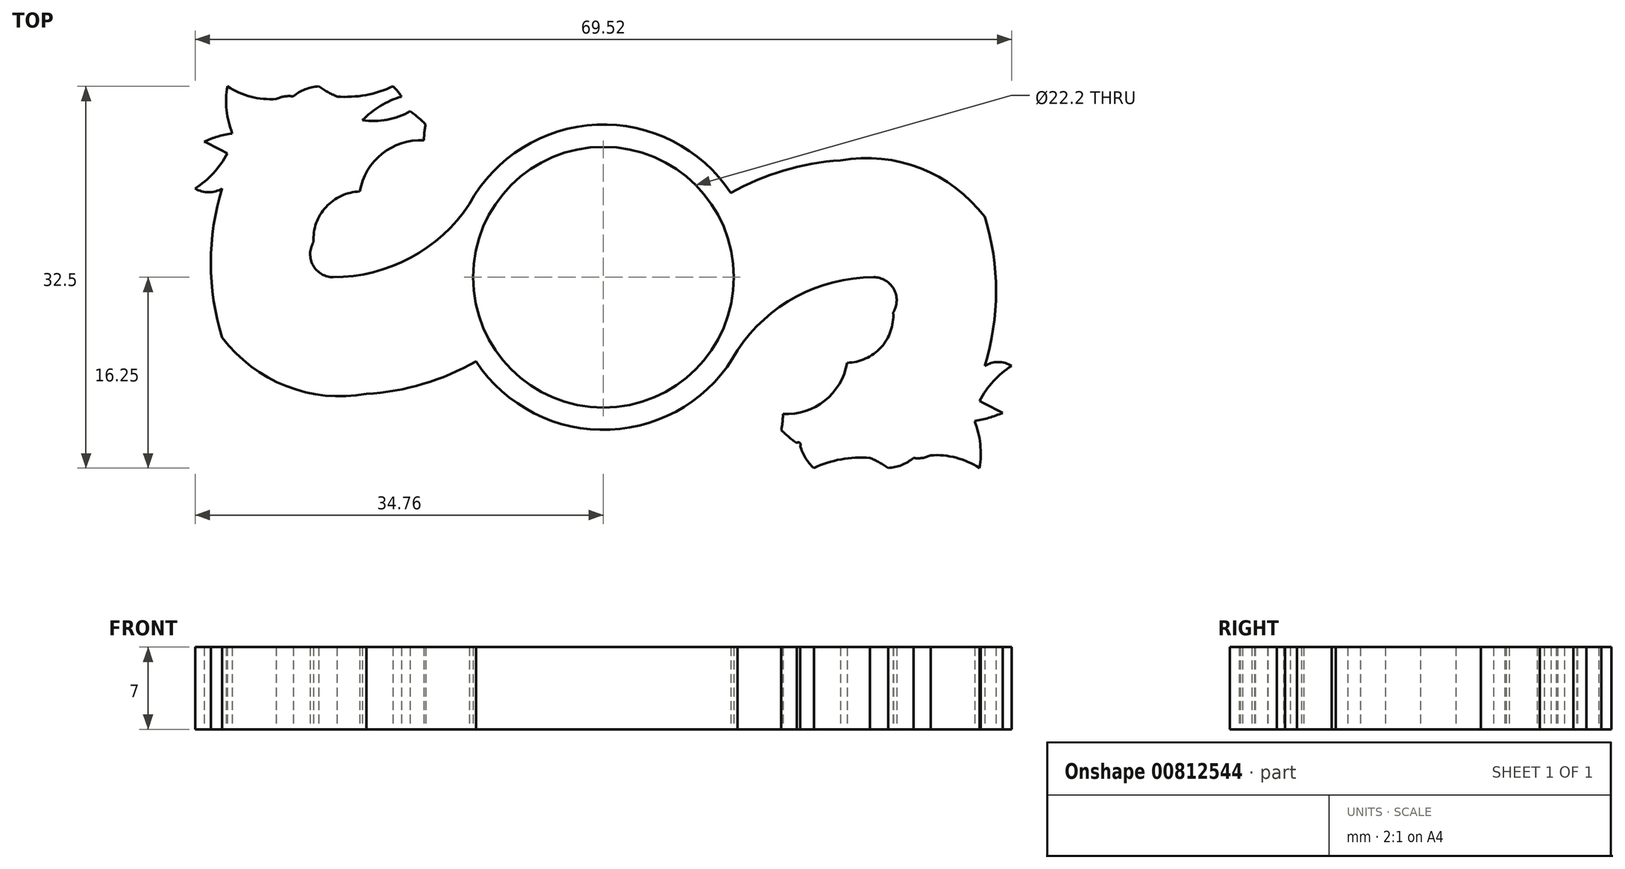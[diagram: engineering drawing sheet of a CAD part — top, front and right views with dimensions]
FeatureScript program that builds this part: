
annotation { "Feature Type Name" : "Feature", "Feature Type Description" : "" }
export const myFeature = defineFeature(function(context is Context, id is Id, definition is map)
    precondition{}
    {
        {
            var Q0;
            Q0=qCreatedBy(makeId("Top.planeOp"),FACE);
            var sketch = newSketch(context, id + "F0", { "sketchPlane" : qUnion([Q0])});
            skCircle(sketch, "E0", {"center": v(0, 0) * mm, "radius": 11.1 * mm});
            skArc(sketch, "E1", {"start": v(-10.84, -7.17) * mm, "mid": v(0.56, -12.99) * mm, "end": v(11.42, -6.21) * mm});
            skPoint(sketch, "E2.center.orphan", {"position": v(-24.05, 0) * mm});
            skEllipticalArc(sketch, "E3", {});
            skEllipticalArc(sketch, "E4", {});
            skEllipticalArc(sketch, "E5.trimOffspring", {});
            skArc(sketch, "E6", {"start": v(-23, 0) * mm, "mid": v(-16.43, 1.65) * mm, "end": v(-11.42, 6.21) * mm});
            skArc(sketch, "E7", {"start": v(-15.28, 11.65) * mm, "mid": v(-18.84, 10.51) * mm, "end": v(-20.74, 7.3) * mm});
            skArc(sketch, "E8", {"start": v(-24.67, 3) * mm, "mid": v(-24.72, 1) * mm, "end": v(-23, 0) * mm});
            skArc(sketch, "E9", {"start": v(-20.74, 7.3) * mm, "mid": v(-23.62, 5.98) * mm, "end": v(-24.67, 3) * mm});
            skArc(sketch, "E10", {"start": v(-17.2, 15.38) * mm, "mid": v(-17.52, 15.84) * mm, "end": v(-17.9, 16.25) * mm});
            skArc(sketch, "E11", {"start": v(-22.68, 15.38) * mm, "mid": v(-20.24, 15.5) * mm, "end": v(-17.9, 16.25) * mm});
            skPoint(sketch, "E11.startSnap0", {"position": v(-17.2, 15.38) * mm});
            skArc(sketch, "E12", {"start": v(-24.25, 16.25) * mm, "mid": v(-23.48, 15.78) * mm, "end": v(-22.68, 15.38) * mm});
            skArc(sketch, "E13", {"start": v(-24.25, 16.25) * mm, "mid": v(-25.39, 16) * mm, "end": v(-26.39, 15.4) * mm});
            skArc(sketch, "E14", {"start": v(-26.39, 15.4) * mm, "mid": v(-27.14, 15.4) * mm, "end": v(-27.85, 15.17) * mm});
            skArc(sketch, "E15", {"start": v(-32.01, 16.25) * mm, "mid": v(-30.02, 15.37) * mm, "end": v(-27.85, 15.17) * mm});
            skArc(sketch, "E16", {"start": v(-32.01, 16.25) * mm, "mid": v(-32.08, 14.21) * mm, "end": v(-31.6, 12.24) * mm});
            skEllipticalArc(sketch, "E17.trimOffspring", {});
            skArc(sketch, "E18", {"start": v(-31.6, 12.24) * mm, "mid": v(-32.82, 11.98) * mm, "end": v(-34, 11.54) * mm});
            skArc(sketch, "E19", {"start": v(-32.01, 10.53) * mm, "mid": v(-33, 11.05) * mm, "end": v(-34, 11.54) * mm});
            skArc(sketch, "E20", {"start": v(-34.76, 7.55) * mm, "mid": v(-33.2, 8.87) * mm, "end": v(-32.01, 10.53) * mm});
            skArc(sketch, "E21", {"start": v(-34.76, 7.55) * mm, "mid": v(-33.6, 7.23) * mm, "end": v(-32.45, 7.55) * mm});
            skArc(sketch, "E22", {"start": v(-32.45, 7.55) * mm, "mid": v(-33.42, 1.2) * mm, "end": v(-32.45, -5.13) * mm});
            skArc(sketch, "E23", {"start": v(-32.45, -5.13) * mm, "mid": v(-27, -9.28) * mm, "end": v(-20.18, -9.94) * mm});
            skPoint(sketch, "E24.start.orphan", {"position": v(-13, 0) * mm});
            skArc(sketch, "E25", {"start": v(-20.18, -9.94) * mm, "mid": v(-15.35, -9.1) * mm, "end": v(-10.84, -7.17) * mm});
            skPoint(sketch, "E26.orphan", {"position": v(-11.42, -6.21) * mm});
            skArc(sketch, "E27.1.0", {"start": v(23, 0) * mm, "mid": v(16.43, -1.65) * mm, "end": v(11.42, -6.21) * mm});
            skArc(sketch, "E27.1.1", {"start": v(24.67, -3) * mm, "mid": v(24.72, -1) * mm, "end": v(23, 0) * mm});
            skArc(sketch, "E27.1.2", {"start": v(20.74, -7.3) * mm, "mid": v(23.62, -5.98) * mm, "end": v(24.67, -3) * mm});
            skArc(sketch, "E27.1.3", {"start": v(15.28, -11.65) * mm, "mid": v(18.84, -10.51) * mm, "end": v(20.74, -7.3) * mm});
            skEllipticalArc(sketch, "E27.1.4", {});
            skEllipticalArc(sketch, "E27.1.5", {});
            skPoint(sketch, "E27.1.7", {"position": v(17.2, -15.38) * mm});
            skArc(sketch, "E27.1.8", {"start": v(16.76, -14.35) * mm, "mid": v(17.2, -15.38) * mm, "end": v(17.9, -16.25) * mm});
            skArc(sketch, "E27.1.9", {"start": v(22.68, -15.38) * mm, "mid": v(20.24, -15.5) * mm, "end": v(17.9, -16.25) * mm});
            skArc(sketch, "E27.1.10", {"start": v(24.25, -16.25) * mm, "mid": v(23.48, -15.78) * mm, "end": v(22.68, -15.38) * mm});
            skArc(sketch, "E27.1.11", {"start": v(24.25, -16.25) * mm, "mid": v(25.39, -16) * mm, "end": v(26.39, -15.4) * mm});
            skArc(sketch, "E27.1.12", {"start": v(26.39, -15.4) * mm, "mid": v(27.14, -15.4) * mm, "end": v(27.85, -15.17) * mm});
            skArc(sketch, "E27.1.13", {"start": v(20.18, 9.94) * mm, "mid": v(15.35, 9.1) * mm, "end": v(10.84, 7.17) * mm});
            skArc(sketch, "E27.1.14", {"start": v(32.45, 5.13) * mm, "mid": v(27, 9.28) * mm, "end": v(20.18, 9.94) * mm});
            skArc(sketch, "E27.1.15", {"start": v(32.45, -7.55) * mm, "mid": v(33.42, -1.2) * mm, "end": v(32.45, 5.13) * mm});
            skArc(sketch, "E27.1.16", {"start": v(34.76, -7.55) * mm, "mid": v(33.6, -7.23) * mm, "end": v(32.45, -7.55) * mm});
            skArc(sketch, "E27.1.17", {"start": v(34.76, -7.55) * mm, "mid": v(33.2, -8.87) * mm, "end": v(32.01, -10.53) * mm});
            skArc(sketch, "E27.1.18", {"start": v(32.01, -10.53) * mm, "mid": v(33, -11.05) * mm, "end": v(34, -11.54) * mm});
            skArc(sketch, "E27.1.19", {"start": v(31.6, -12.24) * mm, "mid": v(32.82, -11.98) * mm, "end": v(34, -11.54) * mm});
            skArc(sketch, "E27.1.20", {"start": v(32.01, -16.25) * mm, "mid": v(32.08, -14.21) * mm, "end": v(31.6, -12.24) * mm});
            skArc(sketch, "E27.1.21", {"start": v(32.01, -16.25) * mm, "mid": v(30.02, -15.37) * mm, "end": v(27.85, -15.17) * mm});
            skArc(sketch, "E28.trimOffspring", {"start": v(10.84, 7.17) * mm, "mid": v(-0.56, 12.99) * mm, "end": v(-11.42, 6.21) * mm});
            skArc(sketch, "E29", {"start": v(16.76, -14.35) * mm, "mid": v(16.7, -14.1) * mm, "end": v(16.45, -14.13) * mm});
            skPoint(sketch, "E30.orphan", {"position": v(-16.76, 14.35) * mm});
            skArc(sketch, "E31", {"start": v(-17.2, 15.38) * mm, "mid": v(-18.99, 14.58) * mm, "end": v(-20.52, 13.36) * mm});
            skArc(sketch, "E32", {"start": v(-20.52, 13.36) * mm, "mid": v(-18.42, 13.4) * mm, "end": v(-16.45, 14.13) * mm});
            const initialGuessF0  = {"E3": [-0.01821213960647583, 0.007251080125570297, 0.6347393649596589, 0.7727263024969507, 0.005441240785988276, 0.0020674565699968753, 0.2580425600777923, 0.2952358654768132], "E4": [-0.013, 0.013858290389180183, -0.32763389716343194, -0.9448047573067685, 0.004450218924481967, 0.0018558373248678793, 5.0540557871872025, 5.402255117798947], "E5.trimOffspring": [-0.023, 0.003, 0, -1, 0.013318096727132796, 0.011934489076924466, 2.4227067274419114, 2.5604830278944943], "E17.trimOffspring": [-0.023, 0.003, 0, -1, 0.013318096727132796, 0.011934489076924466, 3.559735353834658, 3.5600932749172753], "E27.1.4": [0.013, -0.013858290389180185, 0.32763389716343205, 0.9448047573067685, 0.004450218924481967, 0.0018558373248678793, 5.0540557871872025, 5.402255117798946], "E27.1.5": [0.023, -0.003, 0, 1, 0.013318096727132796, 0.011934489076924466, 2.4227067274419114, 2.5604830278944943]};
            skSetInitialGuess(sketch, initialGuessF0);
            skSolve(sketch);
        }
        {
            var Q0;
            Q0 = qSketchRegion(id + "F0", true);
            extrude(context, id + "F1", {"entities" : qUnion([Q0]), "depth" : 7 * mm, "offsetDistance" : 25 * mm});
        }
    });
